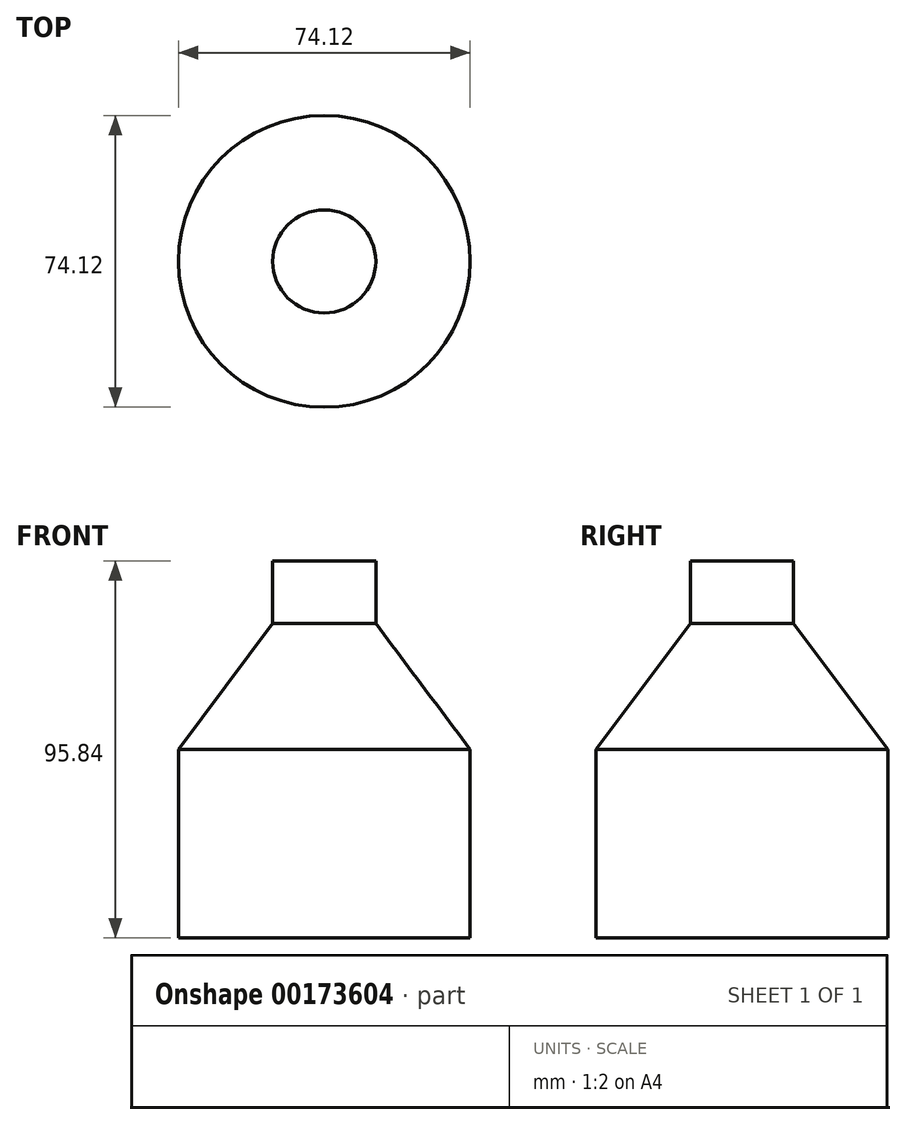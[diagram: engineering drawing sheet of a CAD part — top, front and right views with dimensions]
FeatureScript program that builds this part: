
annotation { "Feature Type Name" : "Feature", "Feature Type Description" : "" }
export const myFeature = defineFeature(function(context is Context, id is Id, definition is map)
    precondition{}
    {
        {
            var Q0;
            Q0=qCreatedBy(makeId("Front.planeOp"),FACE);
            var sketch = newSketch(context, id + "F0", { "sketchPlane" : qUnion([Q0])});
            skLineSegment(sketch, "E0", {"start": v(0, 40.41) * mm, "end": v(0, -55.43) * mm});
            skLineSegment(sketch, "E1", {"start": v(0, -55.43) * mm, "end": v(37.06, -55.43) * mm});
            skLineSegment(sketch, "E2", {"start": v(37.06, -55.43) * mm, "end": v(37.06, -7.5) * mm});
            skLineSegment(sketch, "E3", {"start": v(37.06, -7.5) * mm, "end": v(13.1, 24.44) * mm});
            skLineSegment(sketch, "E4", {"start": v(13.1, 24.44) * mm, "end": v(13.1, 40.41) * mm});
            skLineSegment(sketch, "E5", {"start": v(13.1, 40.41) * mm, "end": v(0, 40.41) * mm});
            skSolve(sketch);
        }
        {
            var Q0;
            Q0=makeQuery(id+"F0.imprint","IMPRINT",FACE,{"disambiguationData":[TD([[makeQuery(id+"F0.imprint","IMPRINT",EDGE,{"derivedFrom":sQuery(id+"F0.wireOp",EDGE,"E0")}),1.0]])]});
            var Q1;
            Q1=sQuery(id+"F0.wireOp",EDGE,"E0");
            revolve(context, id + "F1", {"entities" : qUnion([Q0]), "axis" : qUnion([Q1]), "revolveType" : RevolveType.FULL});
        }
    });
